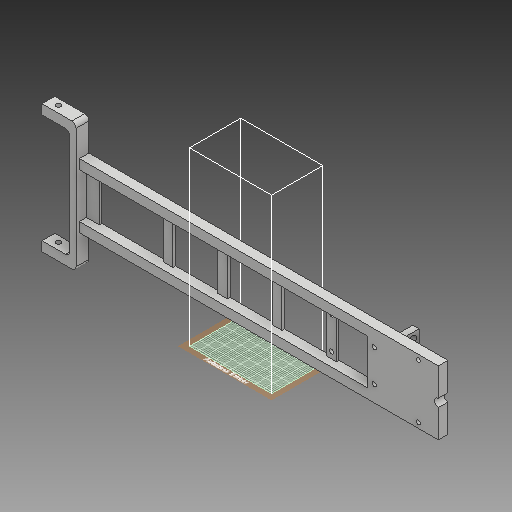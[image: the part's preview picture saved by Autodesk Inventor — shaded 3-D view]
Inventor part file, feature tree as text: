
AUTODESK INVENTOR PART (.ipt)
format: ipt  version: 2018 (Build 220112000, 112)  size: 711,680 bytes
history: native  units: mm
features: sketch x43, extrude x31, fillet x7, hole x6, plane x1
ambient origin geometry x8: Origin, YZ Plane, XZ Plane, XY Plane, X Axis, Y Axis, Z Axis, Center Point
bodies: Solid1 (feature_tree)
feature tree (88):
  extrude  "Extrusion1"  Depth=50.0mm
  hole  "Hole1"  [1 undecoded]
  hole  "Hole2"  [1 undecoded]
  extrude  "Extrusion2"  Depth=25.0mm
  extrude  "Extrusion3"  Depth=25.0mm
  extrude  "Extrusion4"  Depth=5.0mm
  sketch  "Sketch7"  dims[d25=10.0mm d26=5.0mm]
  extrude  "Extrusion5"  Depth=5.0mm
  extrude  "Extrusion6"  Depth=35.0mm
  extrude  "Extrusion7"  Depth=35.0mm
  extrude  "Extrusion8"  Depth=35.0mm
  extrude  "Extrusion9"  Depth=35.0mm TaperAngle=0.0deg
  extrude  "Extrusion10"  Depth=7.5mm TaperAngle=0.0deg
  extrude  "Extrusion11"  Depth=10.0mm
  extrude  "Extrusion12"  Depth=7.5mm
  fillet  "Fillet1"  Radius=7.5mm
  fillet  "Fillet2"  Radius=25.0mm
  fillet  "Fillet3"  Radius=3.0mm
  fillet  "Fillet4"  Radius=3.2mm
  fillet  "Fillet5"  Radius=2.1mm
  fillet  "Fillet6"  Radius=5.5mm
  extrude  "Extrusion13"  Depth=92.5mm TaperAngle=0.0deg
  sketch  "Sketch17"  dims[d58=4.25mm d59=241.0mm d60=0.0mm]
  hole  "Hole3"  [1 undecoded]
  hole  "Hole4"  [1 undecoded]
  extrude  "Extrusion14"  Depth=5.0mm
  extrude  "Extrusion15"  Depth=2.5mm TaperAngle=0.0deg
  extrude  "Extrusion16"  Depth=6.35mm
  extrude  "Extrusion17"  Depth=2.5mm
  extrude  "Extrusion18"  Depth=14.55mm TaperAngle=0.0deg
  extrude  "Extrusion19"  Depth=0.1mm
  extrude  "Extrusion20"  Depth=3.25mm
  extrude  "Extrusion21"  Depth=3.25mm
  hole  "Hole5"  [1 undecoded]
  extrude  "Extrusion22"  Depth=3.6mm
  extrude  "Extrusion23"  Depth=15.0mm
  extrude  "Extrusion24"  Depth=10.0mm TaperAngle=0.0deg
  hole  "Hole6"  [1 undecoded]
  extrude  "Extrusion25"  Depth=100.0mm TaperAngle=0.0deg
  extrude  "Extrusion26"  Depth=5.0mm TaperAngle=0.0deg
  sketch  "Sketch35"  dims[d116=3.3mm d117=3.3mm]
  plane  "Work Plane1"
  sketch  "Sketch36"  dims[d118=3.3mm d119=3.3mm d120=2.0mm d121=0.0mm]
  extrude  "Extrusion27"  Depth=3.3mm
  extrude  "Extrusion28"  Depth=3.3mm
  fillet  "Fillet7"  Radius=2.0mm
  extrude  "Extrusion29"  Depth=42.0mm
  extrude  "Extrusion30"  Depth=21.0mm
  sketch  "Sketch41"  dims[d137=3.5mm]
  sketch  "Sketch42"  dims[d138=21.0mm]
  extrude  "Extrusion31"  Depth=15.825mm
  sketch  "Sketch43"  dims[d139=3.3mm d140=3.3mm d141=3.3mm d142=10.0mm d143=0.0mm d144=7.5mm d145=0.0mm d146=100.0mm d147=0.0mm d148=5.0mm d149=6.0mm d150=4.0mm d151=2.0mm d152=90.0deg d153=15.0mm d154=0.0mm d155=3.75mm d156=100.0mm d157=0.0mm d158=100.0mm d159=0.0mm d160=-0.698132mm d161=5.0mm d162=5.0mm d163=37.5mm d164=0.0mm d165=1.1mm d166=37.5mm d167=0.0mm d168=0.2mm d169=3.0mm d170=5.5mm d171=0.0mm d172=100.0mm d173=0.0mm d174=56.043mm d175=56.043mm d176=74.0mm d177=3.0mm d178=74.0mm d179=3.0mm d180=74.0mm d181=3.0mm d182=74.0mm d183=3.0mm d184=1.0mm d185=0.0mm]
  sketch  "Sketch1"  dims[d0=50.0mm d1=50.0mm]
  sketch  "Sketch2"  dims[d2=240.0mm d3=7.5mm]
  sketch  "Sketch3"  dims[d4=7.5mm d5=7.5mm d6=0.0mm]
  sketch  "Sketch4"  dims[d7=6.35mm d8=6.0mm d9=4.0mm d10=2.0mm d11=90.0deg d12=8.0mm d13=20.594885mm d14=25.0mm]
  sketch  "Sketch5"  dims[d15=3.3mm d16=6.0mm d17=4.0mm d18=2.0mm d19=90.0deg d20=8.0mm d21=20.594885mm d22=25.0mm]
  sketch  "Sketch6"  dims[d23=180.0deg d24=5.0mm]
  sketch  "Sketch8"  dims[d27=17.5mm d28=0.0mm d30=35.0mm]
  sketch  "Sketch9"  dims[d31=35.0mm d32=35.0mm]
  sketch  "Sketch10"  dims[d33=35.0mm d34=35.0mm]
  sketch  "Sketch11"  dims[d35=35.0mm d36=2.0mm d37=0.0mm]
  sketch  "Sketch12"  dims[d38=10.0mm d39=7.5mm d40=0.0mm]
  sketch  "Sketch13"  dims[d41=100.0mm d42=10.0mm]
  sketch  "Sketch14"  dims[d43=7.5mm d44=0.0mm d45=7.5mm d46=7.5mm d47=25.0mm d48=0.0mm d49=3.0mm d50=3.2mm d51=2.1mm d52=5.5mm]
  sketch  "Sketch15"  dims[d53=3.3mm d54=92.5mm d55=0.0mm]
  sketch  "Sketch16"  dims[d56=5.5mm d57=3.3mm]
  sketch  "Sketch18"  dims[d61=4.44mm d62=5.0mm]
  sketch  "Sketch19"  dims[d63=2.5mm d64=91.25mm d65=0.0mm]
  sketch  "Sketch20"  dims[d66=30.0mm d67=6.35mm]
  sketch  "Sketch21"  dims[d68=3.8mm d69=0.0mm d70=2.5mm]
  sketch  "Sketch22"  dims[d71=14.55mm d72=0.0mm d73=14.55mm d74=0.0mm]
  sketch  "Sketch23"  dims[d75=0.1mm d76=0.1mm]
  sketch  "Sketch24"  dims[d77=3.25mm d78=3.25mm]
  sketch  "Sketch25"  dims[d79=3.25mm d80=3.25mm]
  sketch  "Sketch26"  dims[d81=35.0mm d82=10.0mm]
  sketch  "Sketch27"  dims[d83=2.0mm d84=0.0mm d85=3.6mm]
  sketch  "Sketch28"  dims[d86=3.6mm]
  sketch  "Sketch29"  dims[d87=3.3mm d88=6.0mm d89=4.0mm d90=2.0mm d91=90.0deg d92=15.0mm d93=20.594885mm]
  sketch  "Sketch30"  dims[d94=3.3mm d95=6.0mm d96=4.0mm d97=2.0mm d98=90.0deg d99=15.0mm d100=20.594885mm d101=6.0mm]
  sketch  "Sketch31"  dims[d102=20.0mm d103=0.0mm d104=10.0mm d105=0.0mm]
  sketch  "Sketch32"  dims[d106=2.0mm d107=0.0mm d108=4.0mm]
  sketch  "Sketch33"  dims[d109=100.0mm d110=0.0mm d111=100.0mm d112=0.0mm]
  sketch  "Sketch34"  dims[d113=5.0mm d114=2.0mm d115=0.0mm]
  sketch  "Sketch37"  dims[d122=5.5mm d123=0.0mm]
  sketch  "Sketch38"  dims[d124=3.3mm d125=6.0mm d126=4.0mm d127=2.0mm d128=90.0deg d129=8.0mm d130=20.594885mm d131=42.0mm]
  sketch  "Sketch39"  dims[d132=17.0mm d133=21.0mm]
  sketch  "Sketch40"  dims[d135=8.5mm d136=15.825mm]
note: 6 required parameter values undecoded (feature->parameter linkage not recoverable at this tier; creation-order binding heuristic only, values carry confidence <= 0.55)
